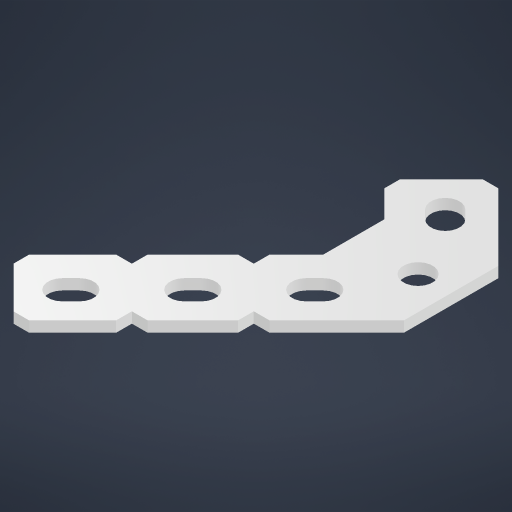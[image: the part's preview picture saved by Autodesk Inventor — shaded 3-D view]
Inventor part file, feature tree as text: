
AUTODESK INVENTOR PART (.ipt)
format: ipt  version: 2024 (Build 280153000, 153)  size: 288,256 bytes
history: native  units: in
note: dims shown in document units (in); Inventor stores cm internally (conversion verified against a paired STEP export)
features: chamfer x1, other x1, split x1, delete_face x1, imported_body x1, sketch x1
ambient origin geometry x8: Origin, YZ Plane, XZ Plane, XY Plane, X Axis, Y Axis, Z Axis, Center Point
bodies: Body1 (feature_tree)
feature tree (6):
  chamfer  "Chamfer1"  [1 undecoded]
  other  "90-Degree Gusset Plate"
  split  "Split1"
  delete_face  "Delete Face1"
  imported_body  "Base1"
  sketch  "Sketch1"
note: 1 required parameter value undecoded (feature->parameter linkage not recoverable at this tier; creation-order binding heuristic only, values carry confidence <= 0.55)
